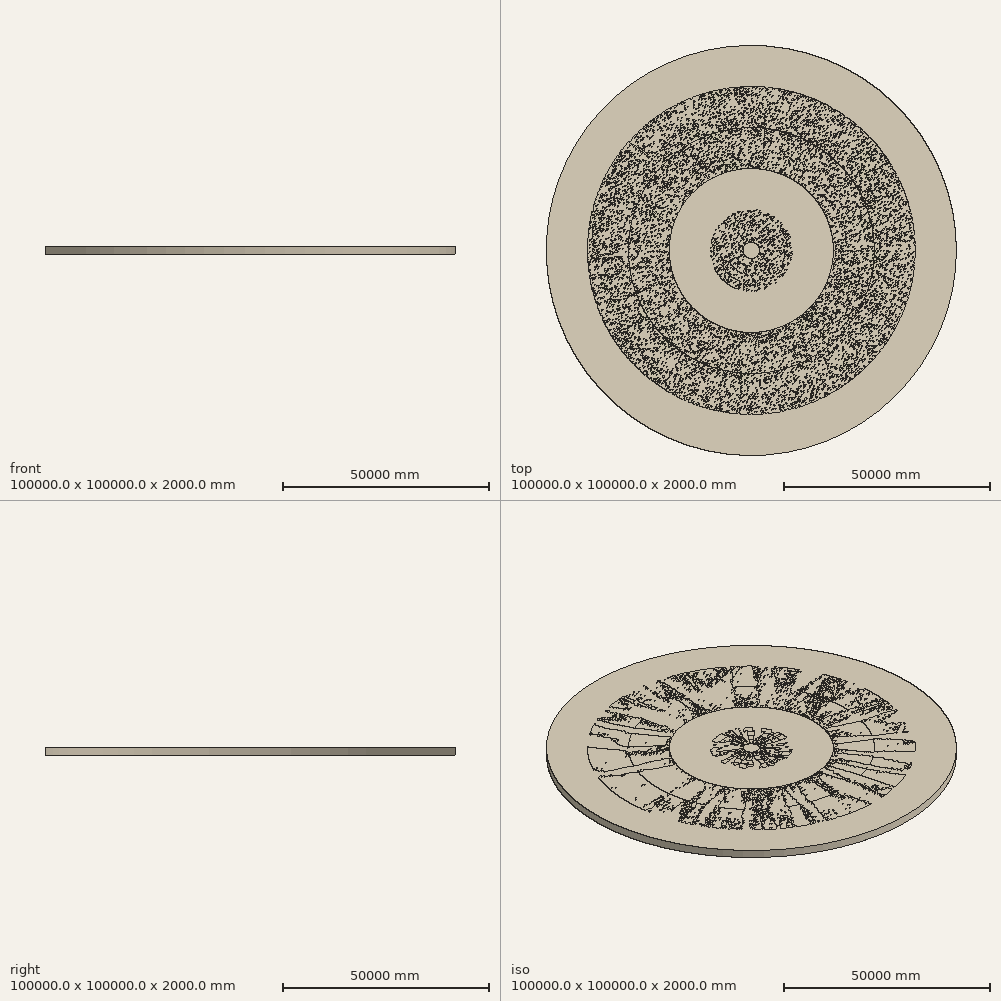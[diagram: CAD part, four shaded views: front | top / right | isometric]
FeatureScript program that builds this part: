
annotation { "Feature Type Name" : "Feature", "Feature Type Description" : "" }
export const myFeature = defineFeature(function(context is Context, id is Id, definition is map)
    precondition{}
    {
        {
            var Q0;
            Q0=qCreatedBy(makeId("Top.planeOp"),FACE);
            var sketch = newSketch(context, id + "F0", { "sketchPlane" : qUnion([Q0])});
            skCircle(sketch, "E0", {"center": v(0, 0) * mm, "radius": 2000 * mm});
            skCircle(sketch, "E1", {"center": v(0, 0) * mm, "radius": 4000 * mm});
            skCircle(sketch, "E2", {"center": v(0, 0) * mm, "radius": 6000 * mm});
            skCircle(sketch, "E3", {"center": v(0, 0) * mm, "radius": 8000 * mm});
            skCircle(sketch, "E4", {"center": v(0, 0) * mm, "radius": 10000 * mm});
            skCircle(sketch, "E5", {"center": v(0, 0) * mm, "radius": 20000 * mm});
            skCircle(sketch, "E6", {"center": v(0, 0) * mm, "radius": 30000 * mm});
            skCircle(sketch, "E7", {"center": v(0, 0) * mm, "radius": 40000 * mm});
            skCircle(sketch, "E8", {"center": v(0, 0) * mm, "radius": 50000 * mm});
            skSolve(sketch);
        }
        {
            var Q0;
            Q0=makeQuery(id+"F0.imprint","IMPRINT",FACE,{"disambiguationData":[TD([[makeQuery(id+"F0.imprint","IMPRINT",EDGE,{"derivedFrom":sQuery(id+"F0.wireOp",EDGE,"E0")}),1.0]])]});
            extrude(context, id + "F1", {"entities" : qUnion([Q0]), "depth" : 2000 * mm, "offsetDistance" : 25 * mm});
        }
        {
            var Q0;
            Q0=makeQuery(id+"F0.imprint","IMPRINT",FACE,{"disambiguationData":[TD([[makeQuery(id+"F0.imprint","IMPRINT",EDGE,{"derivedFrom":sQuery(id+"F0.wireOp",EDGE,"E0")}),-1.0]])]});
            extrude(context, id + "F2", {"entities" : qUnion([Q0]), "depth" : 2000 * mm, "offsetDistance" : 25 * mm});
        }
        {
            var Q0;
            Q0=makeQuery(id+"F0.imprint","IMPRINT",FACE,{"disambiguationData":[TD([[makeQuery(id+"F0.imprint","IMPRINT",EDGE,{"derivedFrom":sQuery(id+"F0.wireOp",EDGE,"E1")}),-1.0]])]});
            extrude(context, id + "F3", {"entities" : qUnion([Q0]), "depth" : 2000 * mm, "offsetDistance" : 25 * mm});
        }
        {
            var Q0;
            Q0=makeQuery(id+"F0.imprint","IMPRINT",FACE,{"disambiguationData":[TD([[makeQuery(id+"F0.imprint","IMPRINT",EDGE,{"derivedFrom":sQuery(id+"F0.wireOp",EDGE,"E2")}),-1.0]])]});
            extrude(context, id + "F4", {"entities" : qUnion([Q0]), "depth" : 2000 * mm, "offsetDistance" : 25 * mm});
        }
        {
            var Q0;
            Q0=makeQuery(id+"F0.imprint","IMPRINT",FACE,{"disambiguationData":[TD([[makeQuery(id+"F0.imprint","IMPRINT",EDGE,{"derivedFrom":sQuery(id+"F0.wireOp",EDGE,"E3")}),-1.0]])]});
            extrude(context, id + "F5", {"entities" : qUnion([Q0]), "depth" : 2000 * mm, "offsetDistance" : 25 * mm});
        }
        {
            var Q0;
            Q0=makeQuery(id+"F0.imprint","IMPRINT",FACE,{"disambiguationData":[TD([[makeQuery(id+"F0.imprint","IMPRINT",EDGE,{"derivedFrom":sQuery(id+"F0.wireOp",EDGE,"E4")}),-1.0]])]});
            var Q1;
            Q1=makeQuery(id+"F0.imprint","IMPRINT",FACE,{"disambiguationData":[TD([[makeQuery(id+"F0.imprint","IMPRINT",EDGE,{"derivedFrom":sQuery(id+"F0.wireOp",EDGE,"E3")}),-1.0]])]});
            var Q2;
            Q2=makeQuery(id+"F0.imprint","IMPRINT",FACE,{"disambiguationData":[TD([[makeQuery(id+"F0.imprint","IMPRINT",EDGE,{"derivedFrom":sQuery(id+"F0.wireOp",EDGE,"E2")}),-1.0]])]});
            var Q3;
            Q3=makeQuery(id+"F0.imprint","IMPRINT",FACE,{"disambiguationData":[TD([[makeQuery(id+"F0.imprint","IMPRINT",EDGE,{"derivedFrom":sQuery(id+"F0.wireOp",EDGE,"E1")}),-1.0]])]});
            var Q4;
            Q4=makeQuery(id+"F0.imprint","IMPRINT",FACE,{"disambiguationData":[TD([[makeQuery(id+"F0.imprint","IMPRINT",EDGE,{"derivedFrom":sQuery(id+"F0.wireOp",EDGE,"E0")}),-1.0]])]});
            extrude(context, id + "F6", {"entities" : qUnion([Q0, Q1, Q2, Q3, Q4]), "depth" : 2000 * mm, "offsetDistance" : 25 * mm});
        }
        {
            var Q0;
            Q0=makeQuery(id+"F0.imprint","IMPRINT",FACE,{"disambiguationData":[TD([[makeQuery(id+"F0.imprint","IMPRINT",EDGE,{"derivedFrom":sQuery(id+"F0.wireOp",EDGE,"E5")}),-1.0]])]});
            extrude(context, id + "F7", {"entities" : qUnion([Q0]), "depth" : 2000 * mm, "offsetDistance" : 25 * mm});
        }
        {
            var Q0;
            Q0=makeQuery(id+"F0.imprint","IMPRINT",FACE,{"disambiguationData":[TD([[makeQuery(id+"F0.imprint","IMPRINT",EDGE,{"derivedFrom":sQuery(id+"F0.wireOp",EDGE,"E6")}),-1.0]])]});
            extrude(context, id + "F8", {"entities" : qUnion([Q0]), "depth" : 2000 * mm, "offsetDistance" : 25 * mm});
        }
        {
            var Q0;
            Q0=makeQuery(id+"F0.imprint","IMPRINT",FACE,{"disambiguationData":[TD([[makeQuery(id+"F0.imprint","IMPRINT",EDGE,{"derivedFrom":sQuery(id+"F0.wireOp",EDGE,"E7")}),-1.0]])]});
            var Q1;
            Q1=makeQuery(id+"F0.imprint","IMPRINT",FACE,{"disambiguationData":[TD([[makeQuery(id+"F0.imprint","IMPRINT",EDGE,{"derivedFrom":sQuery(id+"F0.wireOp",EDGE,"E6")}),-1.0]])]});
            var Q2;
            Q2=makeQuery(id+"F0.imprint","IMPRINT",FACE,{"disambiguationData":[TD([[makeQuery(id+"F0.imprint","IMPRINT",EDGE,{"derivedFrom":sQuery(id+"F0.wireOp",EDGE,"E5")}),-1.0]])]});
            extrude(context, id + "F9", {"entities" : qUnion([Q0, Q1, Q2]), "depth" : 2000 * mm, "offsetDistance" : 25 * mm});
        }
    });
